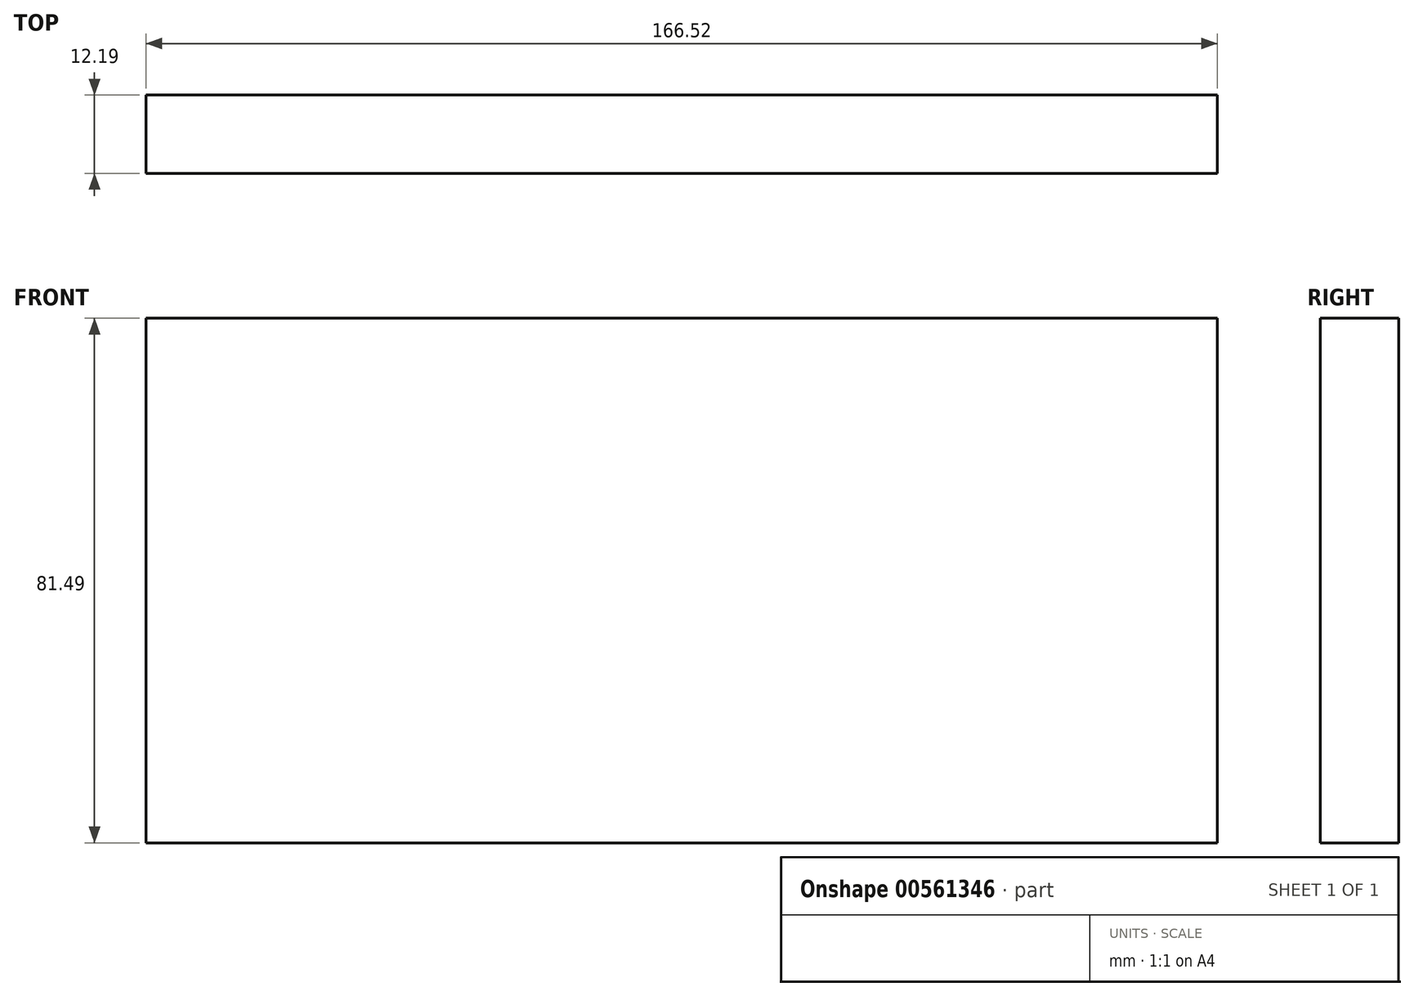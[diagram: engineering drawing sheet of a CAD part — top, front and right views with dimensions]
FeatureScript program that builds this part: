
annotation { "Feature Type Name" : "Feature", "Feature Type Description" : "" }
export const myFeature = defineFeature(function(context is Context, id is Id, definition is map)
    precondition{}
    {
        {
            var Q0;
            Q0=qCreatedBy(makeId("Front.planeOp"),FACE);
            var sketch = newSketch(context, id + "F0", { "sketchPlane" : qUnion([Q0])});
            skLineSegment(sketch, "E0.bottom", {"start": v(-84.44, 39.86) * mm, "end": v(82.08, 39.86) * mm});
            skLineSegment(sketch, "E0.top", {"start": v(-84.44, -41.63) * mm, "end": v(82.08, -41.63) * mm});
            skLineSegment(sketch, "E0.left", {"start": v(-84.44, 39.86) * mm, "end": v(-84.44, -41.63) * mm});
            skLineSegment(sketch, "E0.right", {"start": v(82.08, 39.86) * mm, "end": v(82.08, -41.63) * mm});
            skSolve(sketch);
        }
        {
            var Q0;
            Q0=makeQuery(id+"F0.imprint","IMPRINT",FACE,{"disambiguationData":[TD([[makeQuery(id+"F0.imprint","IMPRINT",EDGE,{"derivedFrom":sQuery(id+"F0.wireOp",EDGE,"E0.bottom")}),-1.0]])]});
            extrude(context, id + "F1", {"entities" : qUnion([Q0]), "depth" : 12.2 * mm, "offsetDistance" : 25.4 * mm});
        }
    });
